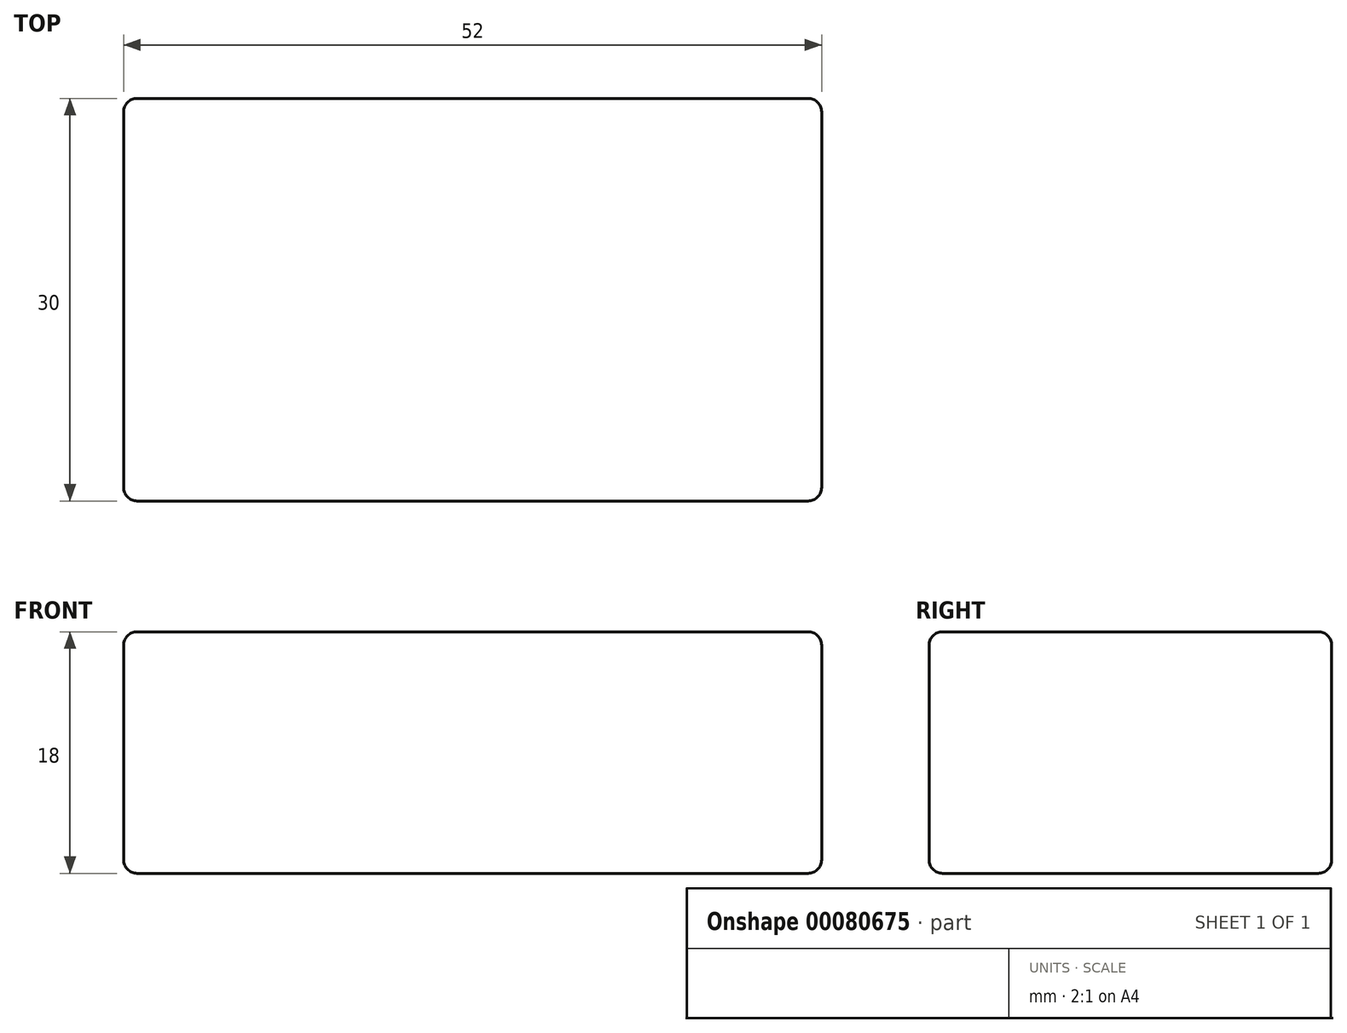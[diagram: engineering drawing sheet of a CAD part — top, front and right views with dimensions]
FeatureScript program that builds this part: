
annotation { "Feature Type Name" : "Feature", "Feature Type Description" : "" }
export const myFeature = defineFeature(function(context is Context, id is Id, definition is map)
    precondition{}
    {
        {
            var Q0;
            Q0=qCreatedBy(makeId("Top.planeOp"),FACE);
            var sketch = newSketch(context, id + "F0", { "sketchPlane" : qUnion([Q0])});
            skLineSegment(sketch, "E0.bottom", {"start": v(26, -15) * mm, "end": v(-26, -15) * mm});
            skLineSegment(sketch, "E0.top", {"start": v(26, 15) * mm, "end": v(-26, 15) * mm});
            skLineSegment(sketch, "E0.left", {"start": v(26, -15) * mm, "end": v(26, 15) * mm});
            skLineSegment(sketch, "E0.right", {"start": v(-26, -15) * mm, "end": v(-26, 15) * mm});
            skPoint(sketch, "E0.middle", {"position": v(0, 0) * mm});
            skSolve(sketch);
        }
        {
            var Q0;
            Q0 = qSketchRegion(id + "F0", true);
            extrude(context, id + "F1", {"entities" : qUnion([Q0]), "depth" : 18 * mm});
        }
        {
            var Q0;
            Q0=makeQuery(id+"F1.opExtrude","SWEPT_EDGE",EDGE,{"disambiguationData":[OSD([sQuery(id+"F0.wireOp",EDGE,"E0.top"),sQuery(id+"F0.wireOp",EDGE,"E0.right")])]});
            var Q1;
            Q1=makeQuery(id+"F1.opExtrude","SWEPT_EDGE",EDGE,{"disambiguationData":[OSD([sQuery(id+"F0.wireOp",EDGE,"E0.top"),sQuery(id+"F0.wireOp",EDGE,"E0.left")])]});
            var Q2;
            Q2=makeQuery(id+"F1.opExtrude","CAP_EDGE",EDGE,{"disambiguationData":[OSD([sQuery(id+"F0.wireOp",EDGE,"E0.top")])],"isStart":false});
            var Q3;
            Q3=makeQuery(id+"F1.opExtrude","CAP_EDGE",EDGE,{"disambiguationData":[OSD([sQuery(id+"F0.wireOp",EDGE,"E0.top")])],"isStart":true});
            var Q4;
            Q4=makeQuery(id+"F1.opExtrude","CAP_EDGE",EDGE,{"disambiguationData":[OSD([sQuery(id+"F0.wireOp",EDGE,"E0.right")])],"isStart":false});
            var Q5;
            Q5=makeQuery(id+"F1.opExtrude","CAP_EDGE",EDGE,{"disambiguationData":[OSD([sQuery(id+"F0.wireOp",EDGE,"E0.right")])],"isStart":true});
            var Q6;
            Q6=makeQuery(id+"F1.opExtrude","SWEPT_EDGE",EDGE,{"disambiguationData":[OSD([sQuery(id+"F0.wireOp",EDGE,"E0.bottom"),sQuery(id+"F0.wireOp",EDGE,"E0.right")])]});
            var Q7;
            Q7=makeQuery(id+"F1.opExtrude","CAP_EDGE",EDGE,{"disambiguationData":[OSD([sQuery(id+"F0.wireOp",EDGE,"E0.bottom")])],"isStart":false});
            var Q8;
            Q8=makeQuery(id+"F1.opExtrude","CAP_EDGE",EDGE,{"disambiguationData":[OSD([sQuery(id+"F0.wireOp",EDGE,"E0.bottom")])],"isStart":true});
            var Q9;
            Q9=makeQuery(id+"F1.opExtrude","CAP_EDGE",EDGE,{"disambiguationData":[OSD([sQuery(id+"F0.wireOp",EDGE,"E0.left")])],"isStart":true});
            var Q10;
            Q10=makeQuery(id+"F1.opExtrude","SWEPT_EDGE",EDGE,{"disambiguationData":[OSD([sQuery(id+"F0.wireOp",EDGE,"E0.bottom"),sQuery(id+"F0.wireOp",EDGE,"E0.left")])]});
            var Q11;
            Q11=makeQuery(id+"F1.opExtrude","CAP_EDGE",EDGE,{"disambiguationData":[OSD([sQuery(id+"F0.wireOp",EDGE,"E0.left")])],"isStart":false});
            fillet(context, id + "F2", {"entities" : qUnion([Q0, Q1, Q2, Q3, Q4, Q5, Q6, Q7, Q8, Q9, Q10, Q11]), "radius" : 1 * mm, "tangentPropagation" : true, "allowEdgeOverflow" : false});
        }
    });
